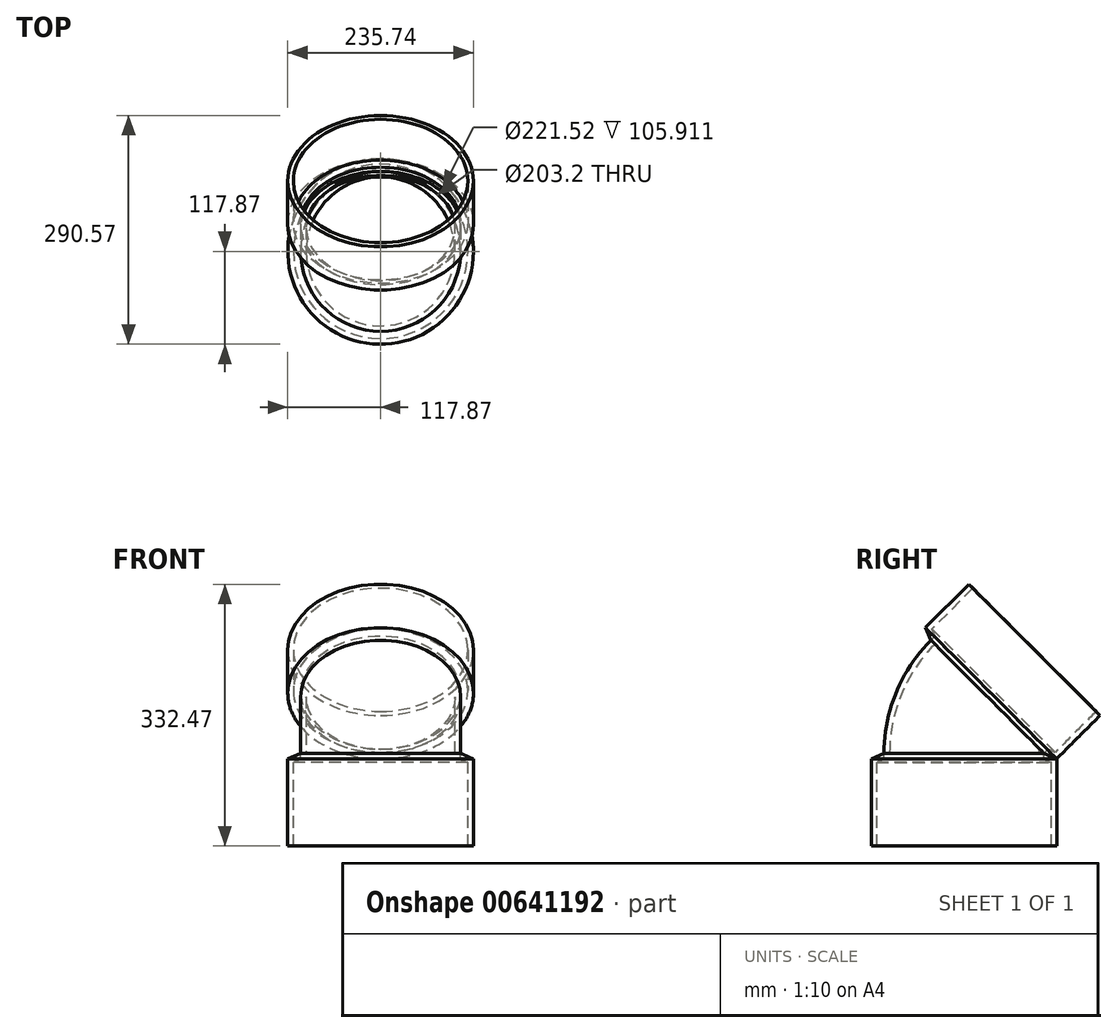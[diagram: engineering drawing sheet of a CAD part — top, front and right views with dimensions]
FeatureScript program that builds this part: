
annotation { "Feature Type Name" : "Feature", "Feature Type Description" : "" }
export const myFeature = defineFeature(function(context is Context, id is Id, definition is map)
    precondition{}
    {
        {
            var Q0;
            Q0=qCreatedBy(makeId("Right.planeOp"),FACE);
            var sketch = newSketch(context, id + "F0", { "sketchPlane" : qUnion([Q0])});
            skLineSegment(sketch, "E0", {"start": v(0, 0) * mm, "end": v(-101.6, 0) * mm});
            skLineSegment(sketch, "E1", {"start": v(0, 0) * mm, "end": v(0, -7.11) * mm});
            skLineSegment(sketch, "E2", {"start": v(0, -7.11) * mm, "end": v(0, -117.68) * mm});
            skLineSegment(sketch, "E3.0", {"start": v(-117.87, -7.11) * mm, "end": v(-117.87, -117.68) * mm});
            skLineSegment(sketch, "E4", {"start": v(-101.6, 0) * mm, "end": v(-117.87, -7.11) * mm});
            skLineSegment(sketch, "E5.0", {"start": v(-110.76, -11.77) * mm, "end": v(-110.76, -117.68) * mm});
            skLineSegment(sketch, "E5.1", {"start": v(-101.6, -7.76) * mm, "end": v(-110.76, -11.77) * mm});
            skLineSegment(sketch, "E6", {"start": v(-117.87, -117.68) * mm, "end": v(-110.76, -117.68) * mm});
            skLineSegment(sketch, "E7", {"start": v(-101.6, 0) * mm, "end": v(-101.6, -7.76) * mm});
            skSolve(sketch);
        }
        {
            var Q0;
            Q0=qCreatedBy(makeId("Top.planeOp"),FACE);
            var sketch = newSketch(context, id + "F1", { "sketchPlane" : qUnion([Q0])});
            skCircle(sketch, "E8", {"center": v(0, 0) * mm, "radius": 101.6 * mm});
            skCircle(sketch, "E9.0", {"center": v(0, 0) * mm, "radius": 94.49 * mm});
            skSolve(sketch);
        }
        {
            var Q0;
            Q0=qCreatedBy(makeId("Right.planeOp"),FACE);
            var sketch = newSketch(context, id + "F2", { "sketchPlane" : qUnion([Q0])});
            skLineSegment(sketch, "E10", {"start": v(0, 0) * mm, "end": v(101.6, 0) * mm});
            skArc(sketch, "E11", {"start": v(29.76, 71.84) * mm, "mid": v(7.73, 38.88) * mm, "end": v(0, 0) * mm});
            skSolve(sketch);
        }
        {
            var Q0;
            Q0=qCreatedBy(makeId("Right.planeOp"),FACE);
            var sketch = newSketch(context, id + "F3", { "sketchPlane" : qUnion([Q0])});
            skLineSegment(sketch, "E12", {"start": v(29.76, 71.84) * mm, "end": v(-42.08, 143.68) * mm});
            skLineSegment(sketch, "E13", {"start": v(29.76, 71.84) * mm, "end": v(34.79, 76.87) * mm});
            skLineSegment(sketch, "E14", {"start": v(34.79, 76.87) * mm, "end": v(112.97, 155.05) * mm});
            skLineSegment(sketch, "E15.0", {"start": v(-49, 159.78) * mm, "end": v(6, 214.79) * mm});
            skLineSegment(sketch, "E16", {"start": v(-49, 159.78) * mm, "end": v(-42.08, 143.68) * mm});
            skLineSegment(sketch, "E17.0", {"start": v(-40.68, 158.04) * mm, "end": v(11.21, 209.93) * mm});
            skLineSegment(sketch, "E18", {"start": v(-36.74, 148.86) * mm, "end": v(-40.68, 158.04) * mm});
            skLineSegment(sketch, "E19", {"start": v(-42.08, 143.68) * mm, "end": v(-36.8, 148.97) * mm});
            skLineSegment(sketch, "E20", {"start": v(6, 214.79) * mm, "end": v(11.21, 209.93) * mm});
            skLineSegment(sketch, "E21", {"start": v(29.76, 71.84) * mm, "end": v(114.9, 71.84) * mm});
            skSolve(sketch);
        }
        {
            var Q0;
            Q0=makeQuery(id+"F0.imprint","IMPRINT",FACE,{"disambiguationData":[TD([[makeQuery(id+"F0.imprint","IMPRINT",EDGE,{"derivedFrom":sQuery(id+"F0.wireOp",EDGE,"E3.0")}),1.0]])]});
            var Q1;
            Q1=sQuery(id+"F0.wireOp",EDGE,"E2");
            revolve(context, id + "F4", {"entities" : qUnion([Q0]), "axis" : qUnion([Q1]), "revolveType" : RevolveType.FULL});
        }
        {
            var Q0;
            Q0=makeQuery(id+"F1.imprint","IMPRINT",FACE,{"disambiguationData":[TD([[makeQuery(id+"F1.imprint","IMPRINT",EDGE,{"derivedFrom":sQuery(id+"F1.wireOp",EDGE,"E8")}),1.0]])]});
            var Q1;
            Q1=sQuery(id+"F2.wireOp",EDGE,"j79Iqw4d-njAS-iAHa-7aqz-3mqtM8yUHerC");
            var Q2;
            Q2=sQuery(id+"F2.wireOp",EDGE,"E11");
            sweep(context, id + "F5", {"profiles" : qUnion([Q0]), "path" : qUnion([Q1, Q2])});
        }
        {
            var Q0;
            Q0=makeQuery(id+"F3.imprint","IMPRINT",FACE,{"disambiguationData":[TD([[makeQuery(id+"F3.imprint","IMPRINT",EDGE,{"derivedFrom":sQuery(id+"F3.wireOp",EDGE,"E15.0")}),-1.0]])]});
            var Q1;
            Q1=sQuery(id+"F3.wireOp",EDGE,"E14");
            revolve(context, id + "F6", {"entities" : qUnion([Q0]), "axis" : qUnion([Q1]), "revolveType" : RevolveType.FULL});
        }
    });
